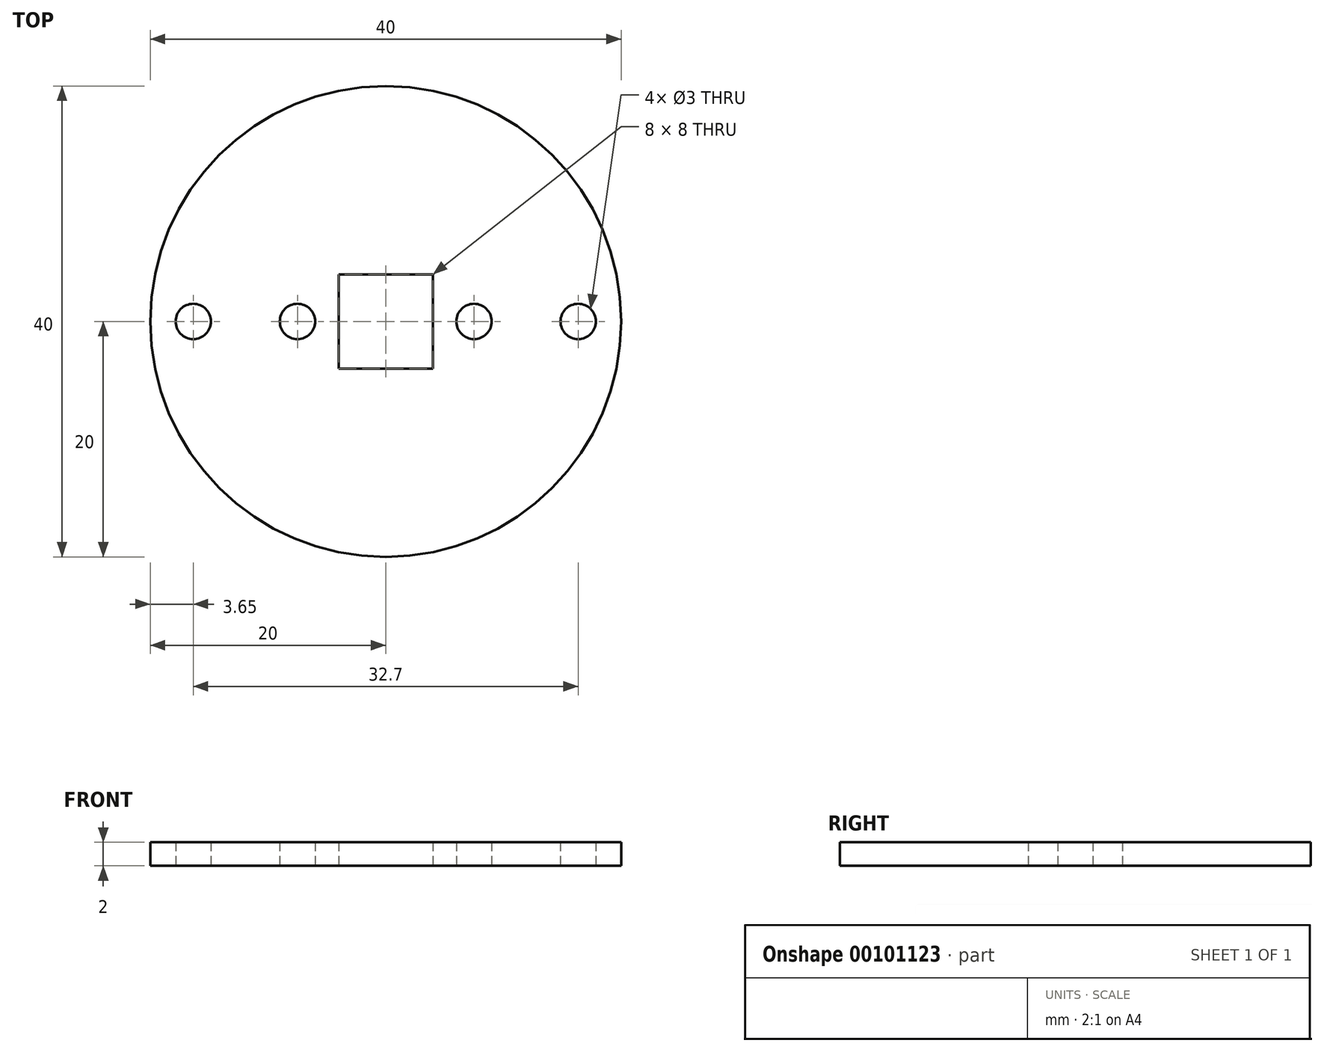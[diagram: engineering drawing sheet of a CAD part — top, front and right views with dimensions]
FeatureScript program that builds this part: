
annotation { "Feature Type Name" : "Feature", "Feature Type Description" : "" }
export const myFeature = defineFeature(function(context is Context, id is Id, definition is map)
    precondition{}
    {
        {
            var Q0;
            Q0=qCreatedBy(makeId("Top.planeOp"),FACE);
            var sketch = newSketch(context, id + "F0", { "sketchPlane" : qUnion([Q0])});
            skLineSegment(sketch, "E0.bottom", {"start": v(-4, 4) * mm, "end": v(4, 4) * mm});
            skLineSegment(sketch, "E0.top", {"start": v(-4, -4) * mm, "end": v(4, -4) * mm});
            skLineSegment(sketch, "E0.left", {"start": v(-4, 4) * mm, "end": v(-4, -4) * mm});
            skLineSegment(sketch, "E0.right", {"start": v(4, 4) * mm, "end": v(4, -4) * mm});
            skPoint(sketch, "E0.middle", {"position": v(0, 0) * mm});
            skLineSegment(sketch, "E1.bottom", {"start": v(-11, 11) * mm, "end": v(11, 11) * mm});
            skLineSegment(sketch, "E1.top", {"start": v(-11, -11) * mm, "end": v(11, -11) * mm});
            skLineSegment(sketch, "E1.left", {"start": v(-11, 11) * mm, "end": v(-11, -11) * mm});
            skLineSegment(sketch, "E1.right", {"start": v(11, 11) * mm, "end": v(11, -11) * mm});
            skCircle(sketch, "E2", {"center": v(0, 0) * mm, "radius": 10 * mm});
            skPoint(sketch, "E3", {"position": v(-7.5, 0) * mm});
            skPoint(sketch, "E3.positionSnap0", {"position": v(-11, 0) * mm});
            skCircle(sketch, "E4", {"center": v(-7.5, 0) * mm, "radius": 1.5 * mm});
            skPoint(sketch, "E5", {"position": v(7.5, 0) * mm});
            skPoint(sketch, "E5.positionSnap0", {"position": v(11, 0) * mm});
            skCircle(sketch, "E6", {"center": v(7.5, 0) * mm, "radius": 1.5 * mm});
            skCircle(sketch, "E7", {"center": v(0, 0) * mm, "radius": 20 * mm});
            skPoint(sketch, "E8", {"position": v(-16.35, 0) * mm});
            skPoint(sketch, "E9", {"position": v(16.35, 0) * mm});
            skSolve(sketch);
        }
        {
            var Q0;
            Q0=makeQuery(id+"F0.imprint","IMPRINT",FACE,{"disambiguationData":[TD([[makeQuery(id+"F0.imprint","IMPRINT",EDGE,{"derivedFrom":sQuery(id+"F0.wireOp",EDGE,"E0.bottom")}),1.0]])]});
            var Q1;
            Q1=makeQuery(id+"F0.imprint","IMPRINT",FACE,{"disambiguationData":[TD([[makeQuery(id+"F0.imprint","IMPRINT",EDGE,{"derivedFrom":sQuery(id+"F0.wireOp",EDGE,"E1.bottom")}),1.0]])]});
            var Q2;
            Q2=makeQuery(id+"F0.imprint","IMPRINT",FACE,{"disambiguationData":[TD([[makeQuery(id+"F0.imprint","IMPRINT",EDGE,{"derivedFrom":sQuery(id+"F0.wireOp",EDGE,"E1.bottom")}),-1.0]])]});
            extrude(context, id + "F1", {"entities" : qUnion([Q0, Q1, Q2]), "depth" : 2 * mm});
        }
        {
            var Q0;
            Q0=sQuery(id+"F0.wireOp",VERTEX,"E8");
            var Q1;
            Q1=sQuery(id+"F0.wireOp",VERTEX,"E9");
            var Q2;
            Q2=makeQuery(id+"F1.opExtrude","SWEPT_BODY",BODY,{"disambiguationData":[OSD([sQuery(id+"F0.wireOp",EDGE,"E0.bottom"),sQuery(id+"F0.wireOp",EDGE,"E0.top"),sQuery(id+"F0.wireOp",EDGE,"E0.left"),sQuery(id+"F0.wireOp",EDGE,"E0.right"),sQuery(id+"F0.wireOp",EDGE,"E4"),sQuery(id+"F0.wireOp",EDGE,"E6"),sQuery(id+"F0.wireOp",EDGE,"E7")])]});
            hole(context, id + "F2", {"style" : HoleStyle.SIMPLE, "endStyle" : HoleEndStyle.BLIND, "oppositeDirection" : true, "holeDiameter" : 3 * mm, "holeDepth" : 25 * mm, "locations" : qUnion([Q0, Q1]), "scope" : qUnion([Q2])});
        }
    });
